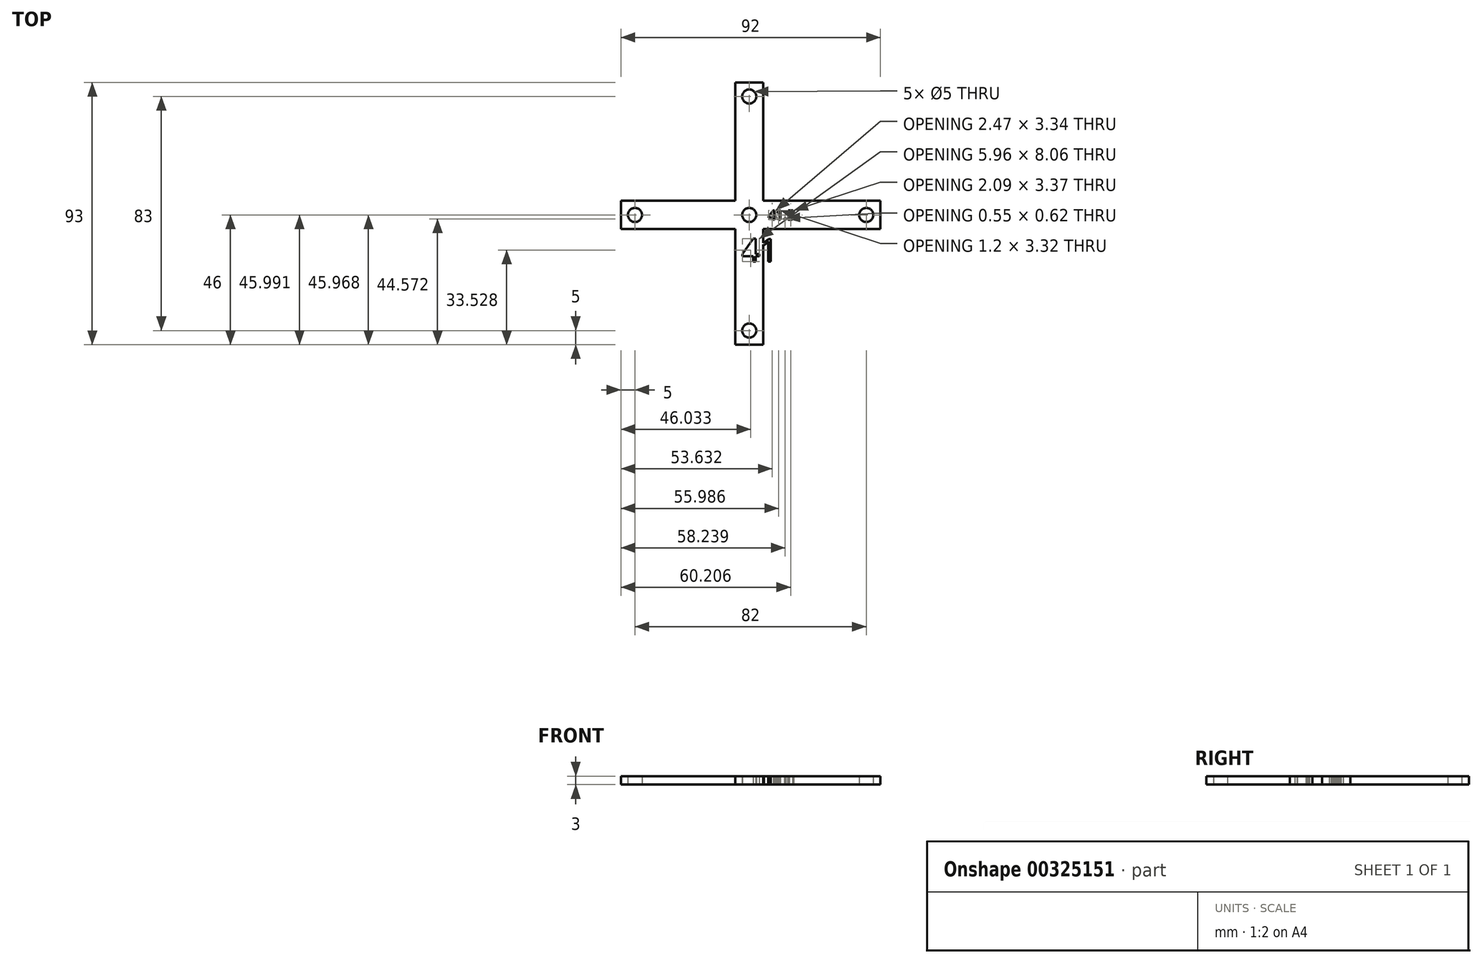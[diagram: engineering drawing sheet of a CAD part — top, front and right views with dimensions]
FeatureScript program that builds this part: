
annotation { "Feature Type Name" : "Feature", "Feature Type Description" : "" }
export const myFeature = defineFeature(function(context is Context, id is Id, definition is map)
    precondition{}
    {
        {
            var Q0;
            Q0=qCreatedBy(makeId("Top.planeOp"),FACE);
            var sketch = newSketch(context, id + "F0", { "sketchPlane" : qUnion([Q0])});
            skLineSegment(sketch, "E0", {"start": v(0, 0) * mm, "end": v(0, 42) * mm, "construction": true});
            skLineSegment(sketch, "E1", {"start": v(0, 0) * mm, "end": v(41.5, 0) * mm, "construction": true});
            skLineSegment(sketch, "E2", {"start": v(0, 0) * mm, "end": v(0, -41) * mm, "construction": true});
            skLineSegment(sketch, "E3", {"start": v(0, 0) * mm, "end": v(-40.5, 0) * mm, "construction": true});
            skCircle(sketch, "E4", {"center": v(0, 42) * mm, "radius": 2.5 * mm});
            skCircle(sketch, "E5", {"center": v(41.5, 0) * mm, "radius": 2.5 * mm});
            skCircle(sketch, "E6", {"center": v(-40.5, 0) * mm, "radius": 2.5 * mm});
            skCircle(sketch, "E7", {"center": v(0, -41) * mm, "radius": 2.5 * mm});
            skLineSegment(sketch, "E8", {"start": v(0, 42) * mm, "end": v(0, 47) * mm});
            skLineSegment(sketch, "E9", {"start": v(0, 47) * mm, "end": v(5, 47) * mm});
            skLineSegment(sketch, "E10", {"start": v(5, 47) * mm, "end": v(5, 5) * mm});
            skLineSegment(sketch, "E11", {"start": v(5, 5) * mm, "end": v(46.5, 5) * mm});
            skLineSegment(sketch, "E12", {"start": v(46.5, 5) * mm, "end": v(46.5, 0) * mm});
            skLineSegment(sketch, "E13", {"start": v(46.5, 0) * mm, "end": v(41.5, 0) * mm});
            skLineSegment(sketch, "E14", {"start": v(0, 0) * mm, "end": v(5, 5) * mm});
            skLineSegment(sketch, "E15", {"start": v(46.5, 0) * mm, "end": v(46.5, -5) * mm});
            skLineSegment(sketch, "E16", {"start": v(46.5, -5) * mm, "end": v(5, -5) * mm});
            skLineSegment(sketch, "E17", {"start": v(5, -5) * mm, "end": v(5, -46) * mm});
            skLineSegment(sketch, "E18", {"start": v(0, -41) * mm, "end": v(0, -46) * mm});
            skLineSegment(sketch, "E19", {"start": v(0, -46) * mm, "end": v(5, -46) * mm});
            skLineSegment(sketch, "E20", {"start": v(0, 47) * mm, "end": v(-5, 47) * mm});
            skLineSegment(sketch, "E21", {"start": v(-5, 47) * mm, "end": v(-5, 5) * mm});
            skLineSegment(sketch, "E22", {"start": v(-5, 5) * mm, "end": v(-45.5, 5) * mm});
            skLineSegment(sketch, "E23", {"start": v(-45.5, 5) * mm, "end": v(-45.5, 0) * mm});
            skLineSegment(sketch, "E24", {"start": v(-45.5, 0) * mm, "end": v(-40.5, 0) * mm});
            skLineSegment(sketch, "E25", {"start": v(-45.5, 0) * mm, "end": v(-45.5, -5) * mm});
            skLineSegment(sketch, "E26", {"start": v(-45.5, -5) * mm, "end": v(-5, -5) * mm});
            skLineSegment(sketch, "E27", {"start": v(-5, -5) * mm, "end": v(-5, -46) * mm});
            skLineSegment(sketch, "E28", {"start": v(-5, -46) * mm, "end": v(0, -46) * mm});
            skCircle(sketch, "E29", {"center": v(0, 0) * mm, "radius": 2.5 * mm});
            skText(sketch, "E30", { "text": "41.5", "fontName": "OpenSans-Regular.ttf"});
            skLineSegment(sketch, "E31", {"start": v(6.8, 1.67) * mm, "end": v(0, 0) * mm, "construction": true});
            skLineSegment(sketch, "E32", {"start": v(6.8, -1.67) * mm, "end": v(0, 0) * mm, "construction": true});
            skText(sketch, "E33", { "text": "41\n", "fontName": "OpenSans-Regular.ttf"});
            const initialGuessF0  = {"E30": [0.0068, -0.00167, 1, 0, 0.00335], "E33": [-0.00268, -0.0165, 1, 0, 0.00808]};
            skSetInitialGuess(sketch, initialGuessF0);
            skSolve(sketch);
        }
        {
            var Q0;
            Q0 = qSketchRegion(id + "F0", true);
            extrude(context, id + "F1", {"entities" : qUnion([Q0]), "depth" : 3 * mm});
        }
    });
